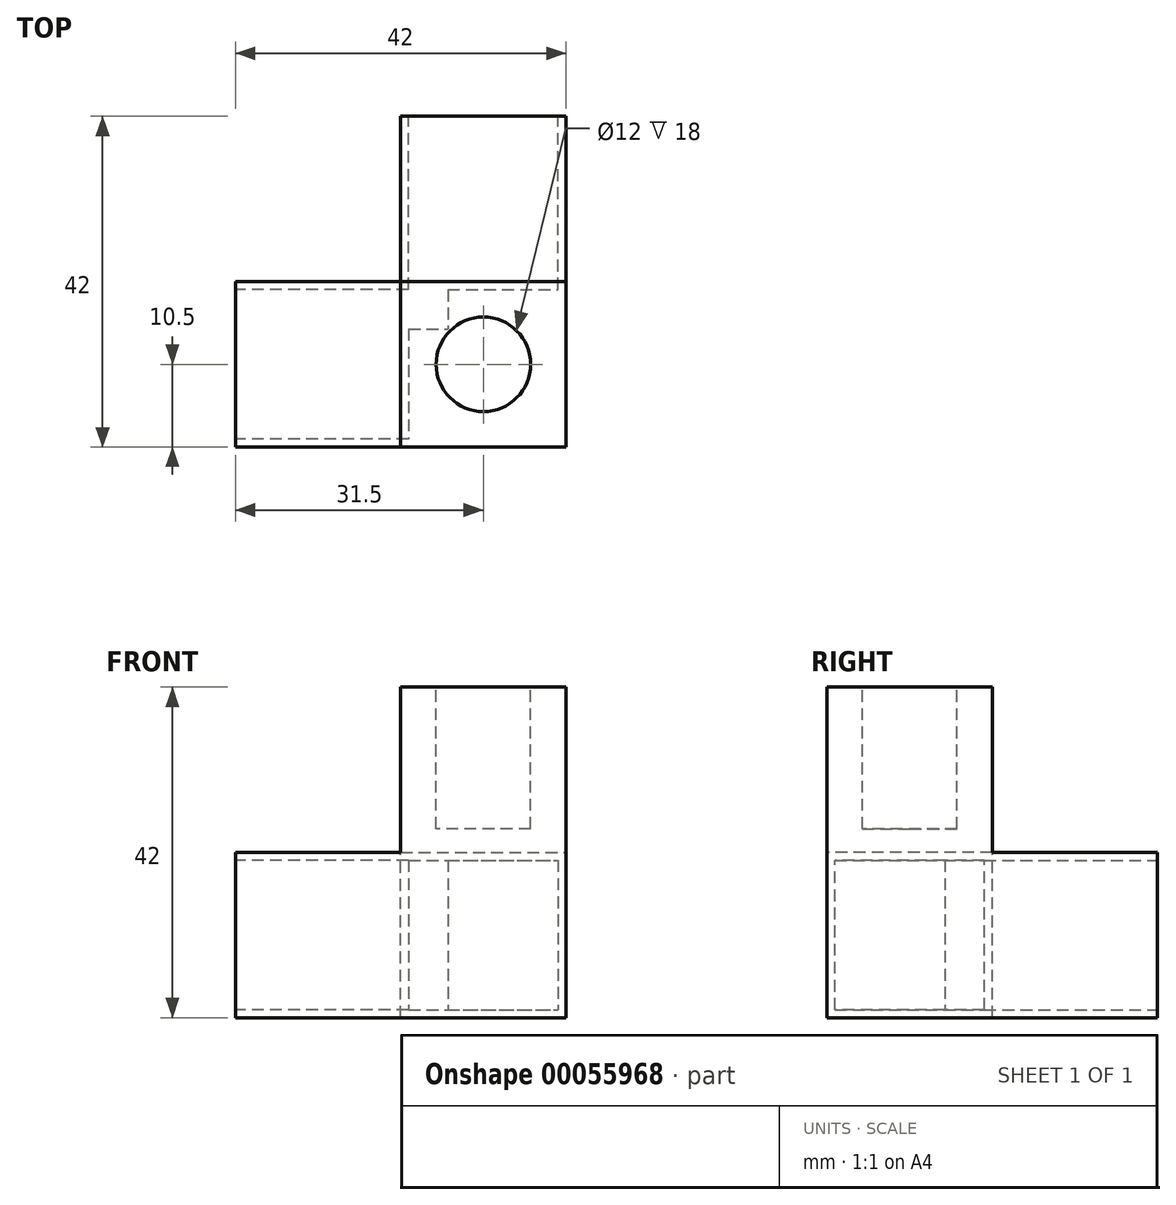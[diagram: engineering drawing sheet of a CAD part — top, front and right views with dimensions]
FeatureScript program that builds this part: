
annotation { "Feature Type Name" : "Feature", "Feature Type Description" : "" }
export const myFeature = defineFeature(function(context is Context, id is Id, definition is map)
    precondition{}
    {
        {
            var Q0;
            Q0=qCreatedBy(makeId("Top.planeOp"),FACE);
            var sketch = newSketch(context, id + "F0", { "sketchPlane" : qUnion([Q0])});
            skLineSegment(sketch, "E0.rect.bottom", {"start": v(21, 21) * mm, "end": v(-21, 21) * mm});
            skLineSegment(sketch, "E0.rect.top", {"start": v(21, -21) * mm, "end": v(-21, -21) * mm});
            skLineSegment(sketch, "E0.rect.left", {"start": v(21, 21) * mm, "end": v(21, -21) * mm});
            skLineSegment(sketch, "E0.rect.right", {"start": v(-21, 21) * mm, "end": v(-21, -21) * mm});
            skPoint(sketch, "E0.rect.middle", {"position": v(0, 0) * mm});
            skSolve(sketch);
        }
        {
            var Q0;
            Q0=makeQuery(id+"F0.imprint","IMPRINT",FACE,{"disambiguationData":[TD([[makeQuery(id+"F0.imprint","IMPRINT",EDGE,{"derivedFrom":sQuery(id+"F0.wireOp",EDGE,"E0.rect.bottom")}),1.0]])]});
            extrude(context, id + "F1", {"entities" : qUnion([Q0]), "depth" : 42 * mm});
        }
        {
            var Q0;
            Q0=makeQuery(id+"F1.opExtrude","CAP_FACE",FACE,{"disambiguationData":[OSD([sQuery(id+"F0.wireOp",EDGE,"E0.rect.bottom"),sQuery(id+"F0.wireOp",EDGE,"E0.rect.top"),sQuery(id+"F0.wireOp",EDGE,"E0.rect.left"),sQuery(id+"F0.wireOp",EDGE,"E0.rect.right")])],"isStart":false});
            var sketch = newSketch(context, id + "F2", { "sketchPlane" : qUnion([Q0])});
            skLineSegment(sketch, "E1.bottom", {"start": v(-21, 21) * mm, "end": v(0, 21) * mm});
            skLineSegment(sketch, "E1.top", {"start": v(-21, 0) * mm, "end": v(0, 0) * mm});
            skLineSegment(sketch, "E1.left", {"start": v(-21, 21) * mm, "end": v(-21, 0) * mm});
            skLineSegment(sketch, "E1.right", {"start": v(0, 21) * mm, "end": v(0, 0) * mm});
            skSolve(sketch);
        }
        {
            var Q0;
            Q0=makeQuery(id+"F2.imprint","IMPRINT",FACE,{"disambiguationData":[TD([[makeQuery(id+"F2.imprint","IMPRINT",EDGE,{"derivedFrom":sQuery(id+"F2.wireOp",EDGE,"E1.bottom")}),1.0]])]});
            extrude(context, id + "F3", {"entities" : qUnion([Q0]), "operationType" : NewBodyOperationType.REMOVE, "endBound" : BoundingType.UP_TO_NEXT, "oppositeDirection" : true, "depth" : 25 * mm});
        }
        {
            var Q0;
            Q0=makeQuery(id+"F1.opExtrude","SWEPT_FACE",FACE,{"disambiguationData":[OSD([sQuery(id+"F0.wireOp",EDGE,"E0.rect.top")])]});
            var sketch = newSketch(context, id + "F4", { "sketchPlane" : qUnion([Q0])});
            skLineSegment(sketch, "E2.bottom", {"start": v(-21, 42) * mm, "end": v(0, 42) * mm});
            skLineSegment(sketch, "E2.top", {"start": v(-21, 21) * mm, "end": v(0, 21) * mm});
            skLineSegment(sketch, "E2.left", {"start": v(-21, 42) * mm, "end": v(-21, 21) * mm});
            skLineSegment(sketch, "E2.right", {"start": v(0, 42) * mm, "end": v(0, 21) * mm});
            skSolve(sketch);
        }
        {
            var Q0;
            Q0=makeQuery(id+"F4.imprint","IMPRINT",FACE,{"disambiguationData":[TD([[makeQuery(id+"F4.imprint","IMPRINT",EDGE,{"derivedFrom":sQuery(id+"F4.wireOp",EDGE,"E2.bottom")}),1.0]])]});
            extrude(context, id + "F5", {"entities" : qUnion([Q0]), "operationType" : NewBodyOperationType.REMOVE, "endBound" : BoundingType.UP_TO_NEXT, "oppositeDirection" : true, "depth" : 25 * mm});
        }
        {
            var Q0;
            Q0=makeQuery(id+"F1.opExtrude","SWEPT_FACE",FACE,{"disambiguationData":[OSD([sQuery(id+"F0.wireOp",EDGE,"E0.rect.left")])]});
            var sketch = newSketch(context, id + "F6", { "sketchPlane" : qUnion([Q0])});
            skLineSegment(sketch, "E3.bottom", {"start": v(21, 42) * mm, "end": v(0, 42) * mm});
            skLineSegment(sketch, "E3.top", {"start": v(21, 21) * mm, "end": v(0, 21) * mm});
            skLineSegment(sketch, "E3.left", {"start": v(21, 42) * mm, "end": v(21, 21) * mm});
            skLineSegment(sketch, "E3.right", {"start": v(0, 42) * mm, "end": v(0, 21) * mm});
            skSolve(sketch);
        }
        {
            var Q0;
            Q0=makeQuery(id+"F6.imprint","IMPRINT",FACE,{"disambiguationData":[TD([[makeQuery(id+"F6.imprint","IMPRINT",EDGE,{"derivedFrom":sQuery(id+"F6.wireOp",EDGE,"E3.bottom")}),1.0]])]});
            extrude(context, id + "F7", {"entities" : qUnion([Q0]), "operationType" : NewBodyOperationType.REMOVE, "endBound" : BoundingType.UP_TO_NEXT, "oppositeDirection" : true, "depth" : 25 * mm});
        }
        {
            var Q0;
            Q0=makeQuery(id+"F1.opExtrude","CAP_FACE",FACE,{"disambiguationData":[OSD([sQuery(id+"F0.wireOp",EDGE,"E0.rect.bottom"),sQuery(id+"F0.wireOp",EDGE,"E0.rect.top"),sQuery(id+"F0.wireOp",EDGE,"E0.rect.left"),sQuery(id+"F0.wireOp",EDGE,"E0.rect.right")])],"isStart":false});
            var sketch = newSketch(context, id + "F8", { "sketchPlane" : qUnion([Q0])});
            skLineSegment(sketch, "E4", {"start": v(0, -21) * mm, "end": v(21, 0) * mm, "construction": true});
            skPoint(sketch, "E5.rect.middle", {"position": v(10.5, -10.5) * mm});
            skCircle(sketch, "E6", {"center": v(10.5, -10.5) * mm, "radius": 6 * mm});
            skSolve(sketch);
        }
        {
            var Q0;
            Q0=makeQuery(id+"F1.opExtrude","SWEPT_FACE",FACE,{"disambiguationData":[OSD([sQuery(id+"F0.wireOp",EDGE,"E0.rect.right")])]});
            var sketch = newSketch(context, id + "F9", { "sketchPlane" : qUnion([Q0])});
            skLineSegment(sketch, "E7", {"start": v(0, 0) * mm, "end": v(21, 21) * mm, "construction": true});
            skLineSegment(sketch, "E8.rect.bottom", {"start": v(20, 1) * mm, "end": v(1, 1) * mm});
            skLineSegment(sketch, "E8.rect.top", {"start": v(20, 20) * mm, "end": v(1, 20) * mm});
            skLineSegment(sketch, "E8.rect.left", {"start": v(20, 1) * mm, "end": v(20, 20) * mm});
            skLineSegment(sketch, "E8.rect.right", {"start": v(1, 1) * mm, "end": v(1, 20) * mm});
            skPoint(sketch, "E8.rect.middle", {"position": v(10.5, 10.5) * mm});
            skSolve(sketch);
        }
        {
            var Q0;
            Q0=makeQuery(id+"F9.imprint","IMPRINT",FACE,{"disambiguationData":[TD([[makeQuery(id+"F9.imprint","IMPRINT",EDGE,{"derivedFrom":sQuery(id+"F9.wireOp",EDGE,"E8.rect.bottom")}),-1.0]])]});
            extrude(context, id + "F10", {"entities" : qUnion([Q0]), "operationType" : NewBodyOperationType.REMOVE, "oppositeDirection" : true, "depth" : 41 * mm});
        }
        {
            var Q0;
            Q0=makeQuery(id+"F1.opExtrude","SWEPT_FACE",FACE,{"disambiguationData":[OSD([sQuery(id+"F0.wireOp",EDGE,"E0.rect.bottom")])]});
            var sketch = newSketch(context, id + "F11", { "sketchPlane" : qUnion([Q0])});
            skLineSegment(sketch, "E9", {"start": v(-21, 21) * mm, "end": v(0, 0) * mm, "construction": true});
            skLineSegment(sketch, "E10.rect.bottom", {"start": v(-1, 20) * mm, "end": v(-20, 20) * mm});
            skLineSegment(sketch, "E10.rect.top", {"start": v(-1, 1) * mm, "end": v(-20, 1) * mm});
            skLineSegment(sketch, "E10.rect.left", {"start": v(-1, 20) * mm, "end": v(-1, 1) * mm});
            skLineSegment(sketch, "E10.rect.right", {"start": v(-20, 20) * mm, "end": v(-20, 1) * mm});
            skPoint(sketch, "E10.rect.middle", {"position": v(-10.5, 10.5) * mm});
            skSolve(sketch);
        }
        {
            var Q0;
            Q0=makeQuery(id+"F11.imprint","IMPRINT",FACE,{"disambiguationData":[TD([[makeQuery(id+"F11.imprint","IMPRINT",EDGE,{"derivedFrom":sQuery(id+"F11.wireOp",EDGE,"E10.rect.bottom")}),1.0]])]});
            extrude(context, id + "F12", {"entities" : qUnion([Q0]), "operationType" : NewBodyOperationType.REMOVE, "oppositeDirection" : true, "depth" : 22 * mm});
        }
        {
            var Q0;
            Q0=makeQuery(id+"F8.imprint","IMPRINT",FACE,{"disambiguationData":[TD([[makeQuery(id+"F8.imprint","IMPRINT",EDGE,{"derivedFrom":sQuery(id+"F8.wireOp",EDGE,"E6")}),1.0]])]});
            extrude(context, id + "F13", {"entities" : qUnion([Q0]), "operationType" : NewBodyOperationType.REMOVE, "oppositeDirection" : true, "depth" : 18 * mm});
        }
        {
            var Q0;
            Q0=makeQuery(id+"F12.boolean.opBoolean","MERGE",FACE,{"derivedFrom":[makeQuery(id+"F10.boolean.opBoolean","COPY",FACE,{"derivedFrom":makeQuery(id+"F10.opExtrude","SWEPT_FACE",FACE,{"disambiguationData":[OSD([sQuery(id+"F9.wireOp",EDGE,"E8.rect.bottom")])]})}),makeQuery(id+"F12.opExtrude","SWEPT_FACE",FACE,{"disambiguationData":[OSD([sQuery(id+"F11.wireOp",EDGE,"E10.rect.top")])]})]});
            var sketch = newSketch(context, id + "F14", { "sketchPlane" : qUnion([Q0])});
            skLineSegment(sketch, "E11.bottom", {"start": v(1, -1) * mm, "end": v(20, -1) * mm});
            skLineSegment(sketch, "E11.top", {"start": v(1, -20) * mm, "end": v(20, -20) * mm});
            skLineSegment(sketch, "E11.left", {"start": v(1, -1) * mm, "end": v(1, -20) * mm});
            skLineSegment(sketch, "E11.right", {"start": v(20, -1) * mm, "end": v(20, -20) * mm});
            skLineSegment(sketch, "E12.top", {"start": v(1, -6) * mm, "end": v(6, -6) * mm});
            skLineSegment(sketch, "E12.right", {"start": v(6, -1) * mm, "end": v(6, -6) * mm});
            skSolve(sketch);
        }
        {
            var Q0;
            {var subQ2=sQuery(id+"F14.wireOp",EDGE,"E11.top");Q0=makeQuery(id+"F14.imprint","IMPRINT",FACE,{"disambiguationData":[TD([[makeQuery(id+"F14.imprint","IMPRINT",EDGE,{"derivedFrom":subQ2}),-1.0]])]});}
            var Q1;
            Q1=makeQuery(id+"F12.boolean.opBoolean","MERGE",FACE,{"derivedFrom":[makeQuery(id+"F10.boolean.opBoolean","COPY",FACE,{"derivedFrom":makeQuery(id+"F10.opExtrude","SWEPT_FACE",FACE,{"disambiguationData":[OSD([sQuery(id+"F9.wireOp",EDGE,"E8.rect.top")])]})}),makeQuery(id+"F12.opExtrude","SWEPT_FACE",FACE,{"disambiguationData":[OSD([sQuery(id+"F11.wireOp",EDGE,"E10.rect.bottom")])]})]});
            extrude(context, id + "F15", {"entities" : qUnion([Q0]), "operationType" : NewBodyOperationType.ADD, "endBound" : BoundingType.UP_TO_NEXT, "endBoundEntityFace" : qUnion([Q1]), "depth" : 5 * mm});
        }
    });
